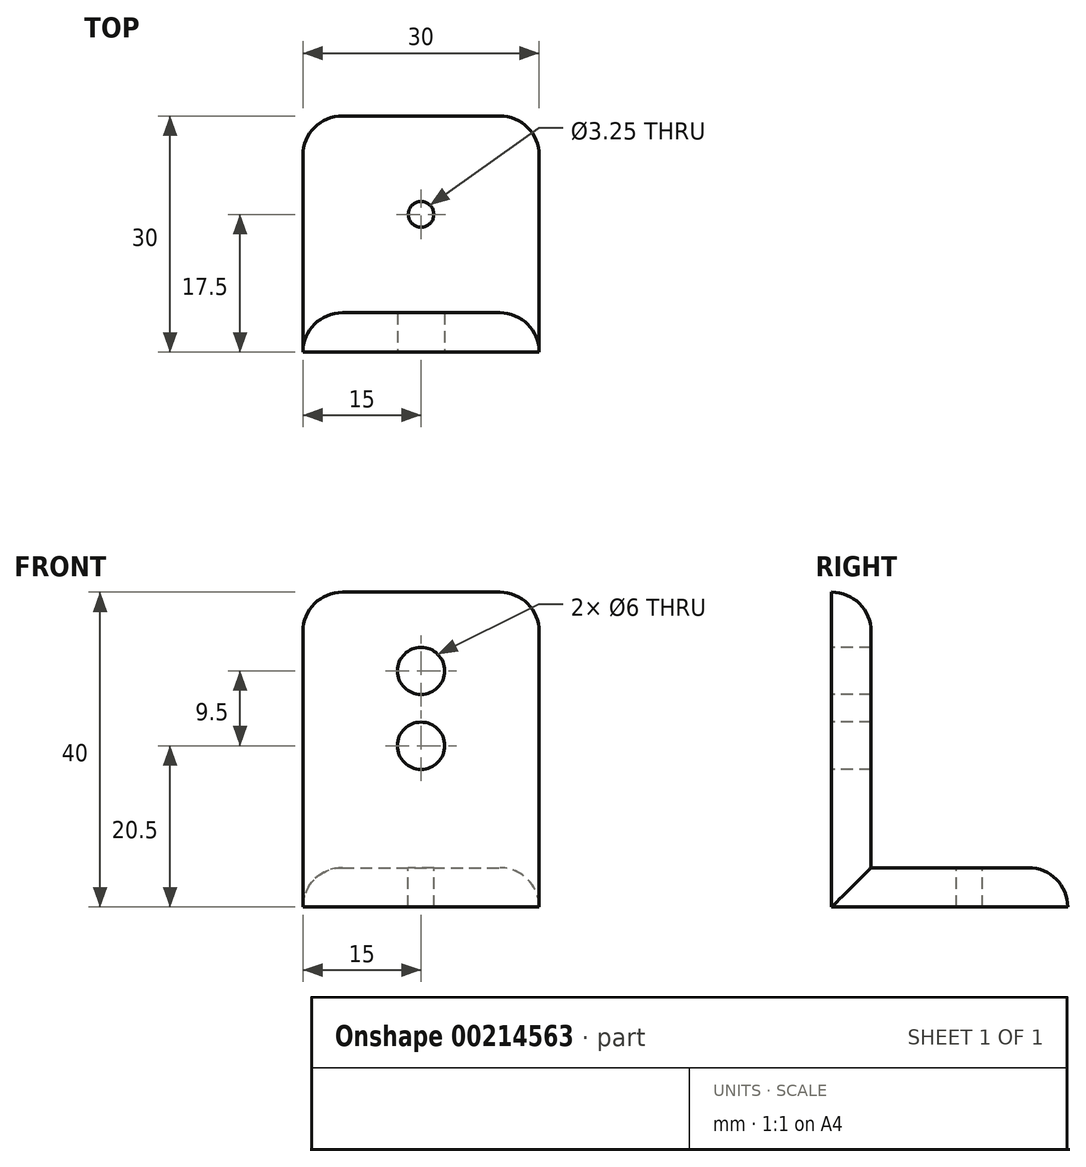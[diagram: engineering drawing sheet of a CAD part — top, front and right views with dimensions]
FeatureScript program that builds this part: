
annotation { "Feature Type Name" : "Feature", "Feature Type Description" : "" }
export const myFeature = defineFeature(function(context is Context, id is Id, definition is map)
    precondition{}
    {
        {
            var Q0;
            Q0=qCreatedBy(makeId("Top.planeOp"),FACE);
            var sketch = newSketch(context, id + "F0", { "sketchPlane" : qUnion([Q0])});
            skLineSegment(sketch, "E0.bottom", {"start": v(-15, 30) * mm, "end": v(15, 30) * mm});
            skLineSegment(sketch, "E0.top", {"start": v(-15, 0) * mm, "end": v(15, 0) * mm});
            skLineSegment(sketch, "E0.left", {"start": v(-15, 30) * mm, "end": v(-15, 0) * mm});
            skLineSegment(sketch, "E0.right", {"start": v(15, 30) * mm, "end": v(15, 0) * mm});
            skSolve(sketch);
        }
        {
            var Q0;
            Q0 = qSketchRegion(id + "F0", true);
            extrude(context, id + "F1", {"entities" : qUnion([Q0]), "depth" : 5 * mm});
        }
        {
            var Q0;
            Q0=makeQuery(id+"F1.opExtrude","SWEPT_FACE",FACE,{"disambiguationData":[OSD([sQuery(id+"F0.wireOp",EDGE,"E0.right")])]});
            var sketch = newSketch(context, id + "F2", { "sketchPlane" : qUnion([Q0])});
            skLineSegment(sketch, "E1.bottom", {"start": v(0, 5) * mm, "end": v(5, 5) * mm});
            skLineSegment(sketch, "E1.top", {"start": v(0, 40) * mm, "end": v(5, 40) * mm});
            skLineSegment(sketch, "E1.left", {"start": v(0, 5) * mm, "end": v(0, 40) * mm});
            skLineSegment(sketch, "E1.right", {"start": v(5, 5) * mm, "end": v(5, 40) * mm});
            skSolve(sketch);
        }
        {
            var Q0;
            Q0=makeQuery(id+"F2.imprint","IMPRINT",FACE,{"disambiguationData":[TD([[makeQuery(id+"F2.imprint","IMPRINT",EDGE,{"derivedFrom":sQuery(id+"F2.wireOp",EDGE,"E1.bottom")}),-1.0]])]});
            extrude(context, id + "F3", {"entities" : qUnion([Q0]), "operationType" : NewBodyOperationType.ADD, "oppositeDirection" : true, "depth" : 30 * mm});
        }
        {
            var Q0;
            Q0=makeQuery(id+"F1.opExtrude","CAP_FACE",FACE,{"disambiguationData":[OSD([sQuery(id+"F0.wireOp",EDGE,"E0.bottom"),sQuery(id+"F0.wireOp",EDGE,"E0.top"),sQuery(id+"F0.wireOp",EDGE,"E0.left"),sQuery(id+"F0.wireOp",EDGE,"E0.right")])],"isStart":false});
            var sketch = newSketch(context, id + "F4", { "sketchPlane" : qUnion([Q0])});
            skCircle(sketch, "E2", {"center": v(0, 17.5) * mm, "radius": 1.62 * mm});
            skPoint(sketch, "E2.centerSnap0", {"position": v(15, 17.5) * mm});
            skSolve(sketch);
        }
        {
            var Q0;
            Q0=makeQuery(id+"F4.imprint","IMPRINT",FACE,{"disambiguationData":[TD([[makeQuery(id+"F4.imprint","IMPRINT",EDGE,{"derivedFrom":sQuery(id+"F4.wireOp",EDGE,"E2")}),1.0]])]});
            var Q1;
            Q1=sQuery(id+"F4.wireOp",EDGE,"E2");
            extrude(context, id + "F5", {"entities" : qUnion([Q0]), "operationType" : NewBodyOperationType.REMOVE, "surfaceEntities" : qUnion([Q1]), "oppositeDirection" : true, "depth" : 25 * mm});
        }
        {
            var Q0;
            Q0=makeQuery(id+"F1.opExtrude","CAP_EDGE",EDGE,{"disambiguationData":[OSD([sQuery(id+"F0.wireOp",EDGE,"E0.bottom")])],"isStart":false});
            var Q1;
            Q1=makeQuery(id+"F1.opExtrude","CAP_EDGE",EDGE,{"disambiguationData":[OSD([sQuery(id+"F0.wireOp",EDGE,"E0.right")])],"isStart":false});
            var Q2;
            Q2=makeQuery(id+"F1.opExtrude","CAP_EDGE",EDGE,{"disambiguationData":[OSD([sQuery(id+"F0.wireOp",EDGE,"E0.left")])],"isStart":false});
            var Q3;
            Q3=makeQuery(id+"F1.opExtrude","SWEPT_EDGE",EDGE,{"disambiguationData":[OSD([sQuery(id+"F0.wireOp",EDGE,"E0.bottom"),sQuery(id+"F0.wireOp",EDGE,"E0.right")])]});
            var Q4;
            Q4=makeQuery(id+"F1.opExtrude","SWEPT_EDGE",EDGE,{"disambiguationData":[OSD([sQuery(id+"F0.wireOp",EDGE,"E0.bottom"),sQuery(id+"F0.wireOp",EDGE,"E0.left")])]});
            fillet(context, id + "F6", {"entities" : qUnion([Q0, Q1, Q2, Q3, Q4]), "radius" : 5 * mm, "tangentPropagation" : true, "allowEdgeOverflow" : false});
        }
        {
            var Q0;
            Q0=makeQuery(id+"F3.boolean.opBoolean","MERGE",FACE,{"derivedFrom":[makeQuery(id+"F1.opExtrude","SWEPT_FACE",FACE,{"disambiguationData":[OSD([sQuery(id+"F0.wireOp",EDGE,"E0.top")])]}),makeQuery(id+"F3.opExtrude","SWEPT_FACE",FACE,{"disambiguationData":[OSD([sQuery(id+"F2.wireOp",EDGE,"E1.left")])]})]});
            var sketch = newSketch(context, id + "F7", { "sketchPlane" : qUnion([Q0])});
            skCircle(sketch, "E3", {"center": v(0, 30) * mm, "radius": 3 * mm});
            skPoint(sketch, "E3.centerSnap0", {"position": v(0, 40) * mm});
            skCircle(sketch, "E4", {"center": v(0, 20.5) * mm, "radius": 3 * mm});
            skSolve(sketch);
        }
        {
            var Q0;
            Q0=makeQuery(id+"F7.imprint","IMPRINT",FACE,{"disambiguationData":[TD([[makeQuery(id+"F7.imprint","IMPRINT",EDGE,{"derivedFrom":sQuery(id+"F7.wireOp",EDGE,"E3")}),1.0]])]});
            var Q1;
            Q1=makeQuery(id+"F7.imprint","IMPRINT",FACE,{"disambiguationData":[TD([[makeQuery(id+"F7.imprint","IMPRINT",EDGE,{"derivedFrom":sQuery(id+"F7.wireOp",EDGE,"E4")}),1.0]])]});
            extrude(context, id + "F8", {"entities" : qUnion([Q0, Q1]), "operationType" : NewBodyOperationType.REMOVE, "oppositeDirection" : true, "depth" : 25 * mm});
        }
        {
            var Q0;
            Q0=makeQuery(id+"F3.opExtrude","CAP_EDGE",EDGE,{"disambiguationData":[OSD([sQuery(id+"F2.wireOp",EDGE,"E1.right")])],"isStart":true});
            var Q1;
            Q1=makeQuery(id+"F3.opExtrude","CAP_EDGE",EDGE,{"disambiguationData":[OSD([sQuery(id+"F2.wireOp",EDGE,"E1.right")])],"isStart":false});
            var Q2;
            Q2=makeQuery(id+"F3.opExtrude","SWEPT_EDGE",EDGE,{"disambiguationData":[OSD([sQuery(id+"F2.wireOp",EDGE,"E1.top"),sQuery(id+"F2.wireOp",EDGE,"E1.right")])]});
            var Q3;
            Q3=makeQuery(id+"F3.opExtrude","CAP_EDGE",EDGE,{"disambiguationData":[OSD([sQuery(id+"F2.wireOp",EDGE,"E1.top")])],"isStart":true});
            var Q4;
            Q4=makeQuery(id+"F3.opExtrude","CAP_EDGE",EDGE,{"disambiguationData":[OSD([sQuery(id+"F2.wireOp",EDGE,"E1.top")])],"isStart":false});
            fillet(context, id + "F9", {"entities" : qUnion([Q0, Q1, Q2, Q3, Q4]), "radius" : 5 * mm, "tangentPropagation" : true, "allowEdgeOverflow" : false});
        }
    });
